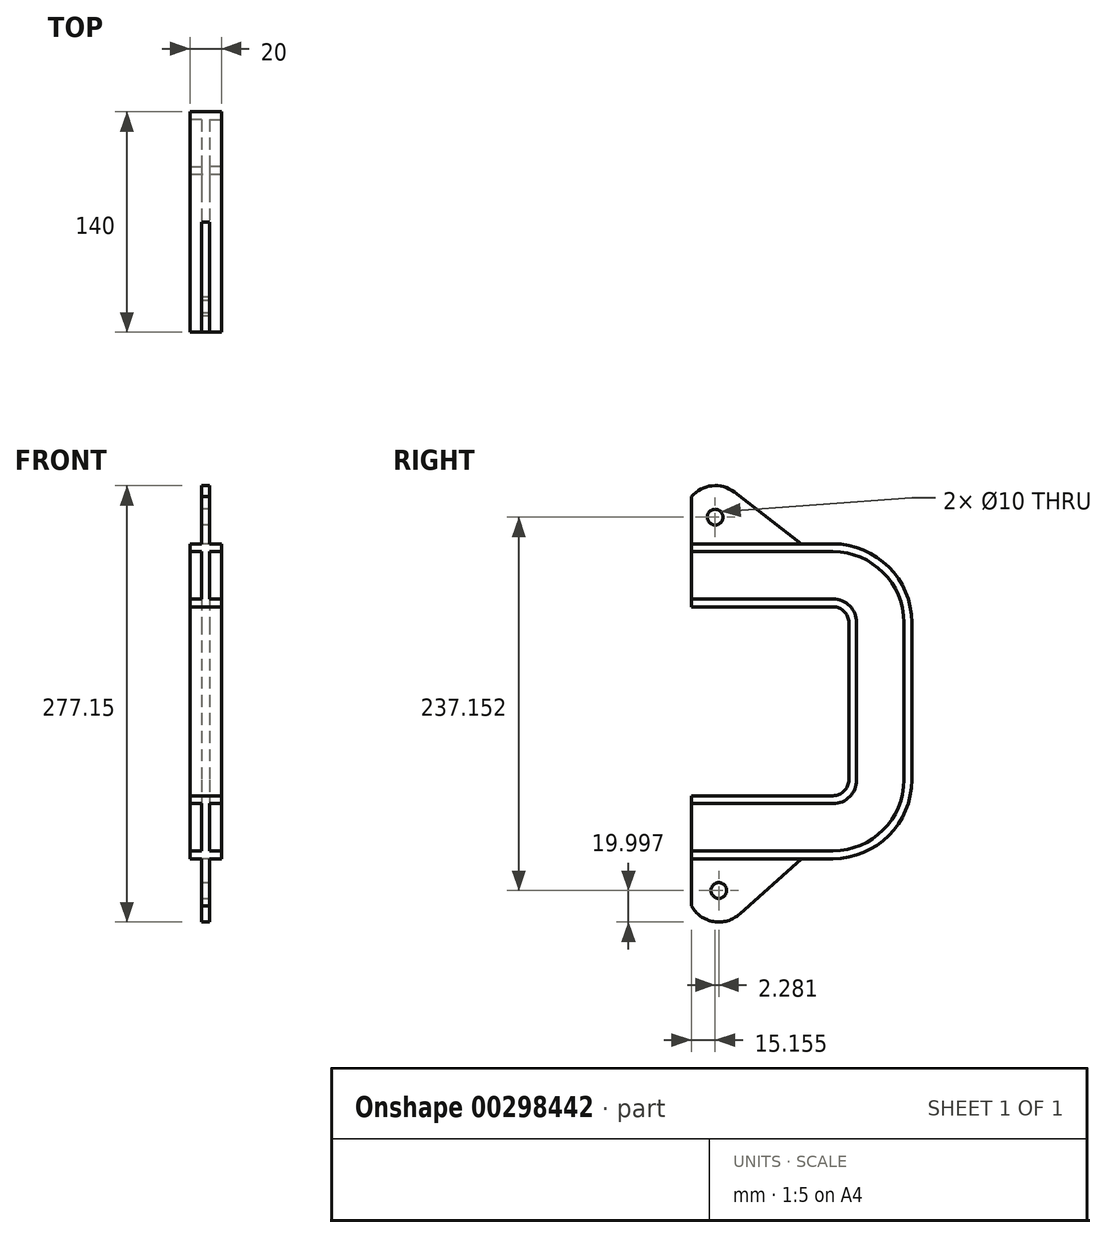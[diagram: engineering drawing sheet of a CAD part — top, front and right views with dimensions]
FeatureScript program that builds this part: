
annotation { "Feature Type Name" : "Feature", "Feature Type Description" : "" }
export const myFeature = defineFeature(function(context is Context, id is Id, definition is map)
    precondition{}
    {
        {
            var Q0;
            Q0=qCreatedBy(makeId("Front.planeOp"),FACE);
            var sketch = newSketch(context, id + "F0", { "sketchPlane" : qUnion([Q0])});
            skLineSegment(sketch, "E0", {"start": v(0, 60) * mm, "end": v(10, 60) * mm});
            skLineSegment(sketch, "E1", {"start": v(10, 60) * mm, "end": v(10, 65) * mm});
            skLineSegment(sketch, "E2", {"start": v(10, 65) * mm, "end": v(2.5, 65) * mm});
            skLineSegment(sketch, "E3", {"start": v(2.5, 65) * mm, "end": v(2.5, 95) * mm});
            skLineSegment(sketch, "E4", {"start": v(2.5, 95) * mm, "end": v(10, 95) * mm});
            skLineSegment(sketch, "E5", {"start": v(10, 95) * mm, "end": v(10, 100) * mm});
            skLineSegment(sketch, "E6", {"start": v(10, 100) * mm, "end": v(0, 100) * mm});
            skLineSegment(sketch, "E7", {"start": v(0, 0) * mm, "end": v(0, 72.24) * mm, "construction": true});
            skLineSegment(sketch, "E8.MirrorCS", {"start": v(-10, 60) * mm, "end": v(-10, 65) * mm});
            skLineSegment(sketch, "E9.MirrorCS", {"start": v(-10, 95) * mm, "end": v(-10, 100) * mm});
            skLineSegment(sketch, "E10.MirrorCS", {"start": v(-2.5, 65) * mm, "end": v(-2.5, 95) * mm});
            skLineSegment(sketch, "E11.MirrorCS", {"start": v(-10, 65) * mm, "end": v(-2.5, 65) * mm});
            skLineSegment(sketch, "E12.MirrorCS", {"start": v(0, 60) * mm, "end": v(-10, 60) * mm});
            skLineSegment(sketch, "E13.MirrorCS", {"start": v(-10, 100) * mm, "end": v(0, 100) * mm});
            skLineSegment(sketch, "E14.MirrorCS", {"start": v(-2.5, 95) * mm, "end": v(-10, 95) * mm});
            skSolve(sketch);
        }
        {
            var Q0;
            Q0=qCreatedBy(makeId("Right.planeOp"),FACE);
            var sketch = newSketch(context, id + "F1", { "sketchPlane" : qUnion([Q0])});
            skLineSegment(sketch, "E15", {"start": v(0, 60) * mm, "end": v(90, 60) * mm});
            skLineSegment(sketch, "E16", {"start": v(100, 50) * mm, "end": v(100, -50) * mm});
            skLineSegment(sketch, "E17", {"start": v(90, -60) * mm, "end": v(0, -60) * mm});
            skPoint(sketch, "E18.visualSharp", {"position": v(100, 60) * mm});
            skArc(sketch, "E18.filletArc", {"start": v(100, 50) * mm, "mid": v(97.07, 57.07) * mm, "end": v(90, 60) * mm});
            skPoint(sketch, "E19.visualSharp", {"position": v(100, -60) * mm});
            skArc(sketch, "E19.filletArc", {"start": v(90, -60) * mm, "mid": v(97.07, -57.07) * mm, "end": v(100, -50) * mm});
            skSolve(sketch);
        }
        {
            var Q0;
            Q0=makeQuery(id+"F0.imprint","IMPRINT",FACE,{"disambiguationData":[TD([[makeQuery(id+"F0.imprint","IMPRINT",EDGE,{"derivedFrom":sQuery(id+"F0.wireOp",EDGE,"E0")}),1.0]])]});
            var Q1;
            Q1=sQuery(id+"F1.wireOp",EDGE,"E15");
            var Q2;
            Q2=sQuery(id+"F1.wireOp",EDGE,"E18.filletArc");
            var Q3;
            Q3=sQuery(id+"F1.wireOp",EDGE,"E16");
            var Q4;
            Q4=sQuery(id+"F1.wireOp",EDGE,"E19.filletArc");
            var Q5;
            Q5=sQuery(id+"F1.wireOp",EDGE,"E17");
            sweep(context, id + "F2", {"profiles" : qUnion([Q0]), "path" : qUnion([Q1, Q2, Q3, Q4, Q5])});
        }
        {
            var Q0;
            Q0=qCreatedBy(makeId("Right.planeOp"),FACE);
            var sketch = newSketch(context, id + "F3", { "sketchPlane" : qUnion([Q0])});
            skLineSegment(sketch, "E20", {"start": v(0, 0) * mm, "end": v(0, 100) * mm, "construction": true});
            skLineSegment(sketch, "E21", {"start": v(0, 100) * mm, "end": v(70, 100) * mm});
            skLineSegment(sketch, "E22", {"start": v(0, 100) * mm, "end": v(0, 130) * mm});
            skLineSegment(sketch, "E23", {"start": v(70, 100) * mm, "end": v(27.35, 132.8) * mm});
            skArc(sketch, "E24", {"start": v(27.35, 132.8) * mm, "mid": v(13.12, 136.84) * mm, "end": v(0, 130) * mm});
            skSolve(sketch);
        }
        {
            var Q0;
            Q0 = qSketchRegion(id + "F3", true);
            extrude(context, id + "F4", {"entities" : qUnion([Q0]), "operationType" : NewBodyOperationType.ADD, "endBound" : BoundingType.SYMMETRIC, "depth" : 5 * mm});
        }
        {
            var Q0;
            Q0=makeQuery(id+"F4.opExtrude","CAP_FACE",FACE,{"disambiguationData":[OSD([sQuery(id+"F3.wireOp",EDGE,"E21"),sQuery(id+"F3.wireOp",EDGE,"E22"),sQuery(id+"F3.wireOp",EDGE,"E23"),sQuery(id+"F3.wireOp",EDGE,"E24")])],"isStart":true});
            var sketch = newSketch(context, id + "F5", { "sketchPlane" : qUnion([Q0])});
            skCircle(sketch, "E25", {"center": v(-15.15, 116.95) * mm, "radius": 5 * mm});
            skSolve(sketch);
        }
        {
            var Q0;
            Q0=makeQuery(id+"F5.imprint","IMPRINT",FACE,{"disambiguationData":[TD([[makeQuery(id+"F5.imprint","IMPRINT",EDGE,{"derivedFrom":sQuery(id+"F5.wireOp",EDGE,"E25")}),1.0]])]});
            extrude(context, id + "F6", {"entities" : qUnion([Q0]), "operationType" : NewBodyOperationType.REMOVE, "oppositeDirection" : true, "depth" : 25.4 * mm});
        }
        {
            var Q0;
            Q0=qCreatedBy(makeId("Right.planeOp"),FACE);
            var sketch = newSketch(context, id + "F7", { "sketchPlane" : qUnion([Q0])});
            skLineSegment(sketch, "E26", {"start": v(0, 0) * mm, "end": v(0, -100) * mm, "construction": true});
            skLineSegment(sketch, "E27", {"start": v(0, -100) * mm, "end": v(70, -100) * mm});
            skLineSegment(sketch, "E28", {"start": v(0, -100) * mm, "end": v(0, -130) * mm});
            skLineSegment(sketch, "E29", {"start": v(70, -100) * mm, "end": v(30.77, -135.1) * mm});
            skArc(sketch, "E30", {"start": v(0, -130) * mm, "mid": v(14.16, -139.93) * mm, "end": v(30.77, -135.1) * mm});
            skSolve(sketch);
        }
        {
            var Q0;
            Q0 = qSketchRegion(id + "F7", true);
            extrude(context, id + "F8", {"entities" : qUnion([Q0]), "operationType" : NewBodyOperationType.ADD, "endBound" : BoundingType.SYMMETRIC, "depth" : 5 * mm});
        }
        {
            var Q0;
            Q0=makeQuery(id+"F8.opExtrude","CAP_FACE",FACE,{"disambiguationData":[OSD([sQuery(id+"F7.wireOp",EDGE,"E27"),sQuery(id+"F7.wireOp",EDGE,"E28"),sQuery(id+"F7.wireOp",EDGE,"E29"),sQuery(id+"F7.wireOp",EDGE,"E30")])],"isStart":false});
            var sketch = newSketch(context, id + "F9", { "sketchPlane" : qUnion([Q0])});
            skCircle(sketch, "E31", {"center": v(17.44, -120.2) * mm, "radius": 5 * mm});
            skSolve(sketch);
        }
        {
            var Q0;
            Q0 = qSketchRegion(id + "F9", true);
            extrude(context, id + "F10", {"entities" : qUnion([Q0]), "operationType" : NewBodyOperationType.REMOVE, "oppositeDirection" : true, "depth" : 25.4 * mm});
        }
    });
